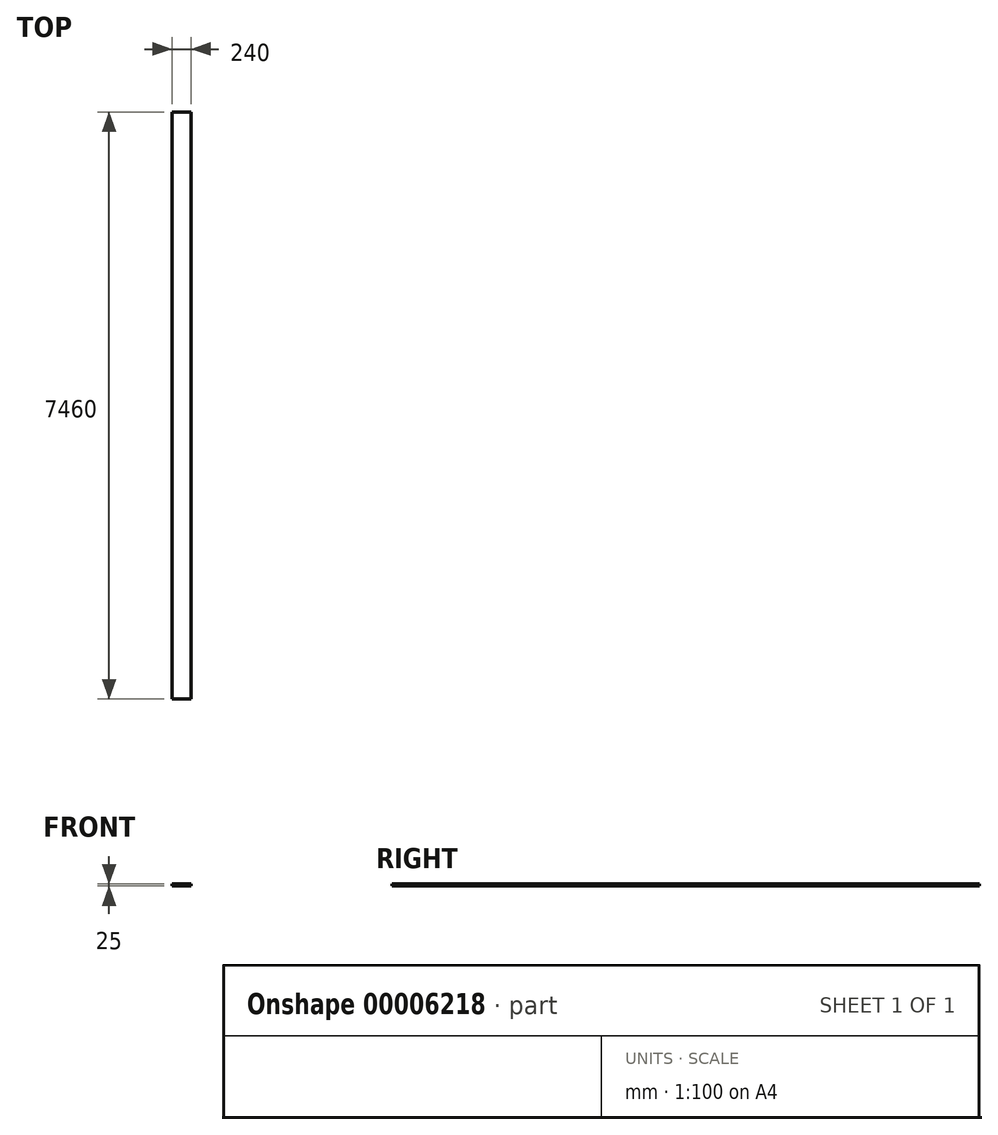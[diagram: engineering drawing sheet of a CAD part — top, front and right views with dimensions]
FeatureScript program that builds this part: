
annotation { "Feature Type Name" : "Feature", "Feature Type Description" : "" }
export const myFeature = defineFeature(function(context is Context, id is Id, definition is map)
    precondition{}
    {
        {
            var Q0;
            Q0=qCreatedBy(makeId("Top.planeOp"),FACE);
            var sketch = newSketch(context, id + "F0", { "sketchPlane" : qUnion([Q0])});
            skLineSegment(sketch, "E0.rect.bottom", {"start": v(120, 3730) * mm, "end": v(-120, 3730) * mm});
            skLineSegment(sketch, "E0.rect.top", {"start": v(120, -3730) * mm, "end": v(-120, -3730) * mm});
            skLineSegment(sketch, "E0.rect.left", {"start": v(120, 3730) * mm, "end": v(120, -3730) * mm});
            skLineSegment(sketch, "E0.rect.right", {"start": v(-120, 3730) * mm, "end": v(-120, -3730) * mm});
            skPoint(sketch, "E0.rect.middle", {"position": v(0, 0) * mm});
            skSolve(sketch);
        }
        {
            var Q0;
            Q0 = qSketchRegion(id + "F0", true);
            extrude(context, id + "F1", {"entities" : qUnion([Q0]), "depth" : 25 * mm});
        }
    });
